# Revit family: Toilet-Intelligent-Floor_Mount-KOHLER-INNATE-K-8340T_1
name_source: partatom
category: Plumbing Fixtures
revit_build: Autodesk Revit 2017 (Build: 20160225_1515(x64)
units: mm (PartAtom-declared; Revit-internal decimal feet)

## family parameters
Cut with Voids When Loaded = No
Host = Face
OmniClass Number = 23.31.19.00
OmniClass Title = Toilets
Part Type = Normal
Room Calculation Point = No
Round Connector Dimension = Use Diameter
Shared = No

## types (8) — shared parameters
ADA Compliant = No
Apparent Load = 0 VA
Assembly Code = D2010100
CW Connection = Yes
Cold Water Inlet = Cold Water Inlet
Date Modified = 12/31/2020
Default Elevation = 0"
Electrical Connector = Yes
Electrical Note = One Dedicated Circuite Requiered
Finish = Kohler-Vitreous_China-0-White
Flow Rate = 0 GPM
Flush Rate- GPF = 1.45 GPF
Flush Rate- LPF = 5.5 LPF
HW Connection = No
Height = 21 5/8"
Hot Water Inlet = Hot Water Inlet
Length = 28 3/8"
Manufacturer = KOHLER Co.
Master Format 2014 = 22 41 13.13
Master Format 2014 Name = Residential Water Closets
Material = Vitreous China
Pressure = 0.00 psi
Product Name = INNATE
Rough-In = 12"
Seat Included = Yes
Vent Connection = No
Voltage = 220 V
Waste Connection = Yes
Waste Water Outlet = Waste Water Outlet
WaterSense Certified = No
Width = 17"

## per-type parameters (varying)
| type | Description | Model | Product Documentation Link | Product Page URL | Seat Material | Type | URL |
| 2,0-White | Smart Toilet (Kohler White) S305 | K-8340T-2-0 | https://files.kohler.com.cn | https://www.kohler.com.cn | Kohler-Plastic-0-White | 3 | http://www.kohler.com.cn |
| 2WT,0-White | Smart Toilet (Moonlight White) S305 | K-8340T-2WT-0 | https://files.kohler.com.cn | https://www.kohler.com.cn | Kohler-Plastic-0-White | 5 | https://www.kohler.com.cn |
| 2SG,0-White |  | K-8340T-2SG-0 | https://files.kohler.com.cn |  | Kohler-Plastic-RGD-Rose_Gold | 7 | http://www.kohler.com.cn |
| 2XP,0-White | Smart Toilet (Cloud Smart Version) S305 | K-8340T-2XP-0 | https://files.kohler.com.cn | https://www.kohler.com.cn | Kohler-Plastic-RGD-Rose_Gold | 1 | http://www.kohler.com.cn |
| 2EX,0-White | Smart Toilet (Kohler White) S305EX | K-8340T-2EX-0 | https://files.kohler.com.cn | https://www.kohler.com.cn | Kohler-Plastic-0-White | 4 | http://www.kohler.com.cn |
| 2EXWT,0-White | Smart Toilet (Moonlight White) S305EX | K-8340T-2EXWT-0 | https://files.kohler.com.cn | https://www.kohler.com.cn | Kohler-Plastic-0-White | 6 | http://www.kohler.com.cn |
| 2EXSG,0-White |  | K-8340T-2EXSG-0 |  |  | Kohler-Plastic-RGD-Rose_Gold | 8 | http://www.kohler.com.cn |
| 2XPEX,0-White | Smart Toilet (Cloud Smart Version) S305EX | K-8340T-2XPEX-0 | https://files.kohler.com.cn | https://www.kohler.com.cn | Kohler-Plastic-RGD-Rose_Gold | 2 | http://www.kohler.com.cn |

## geometry (parser evidence)
native form markers: Sweep x5
no freeform markers — native parametric forms only
